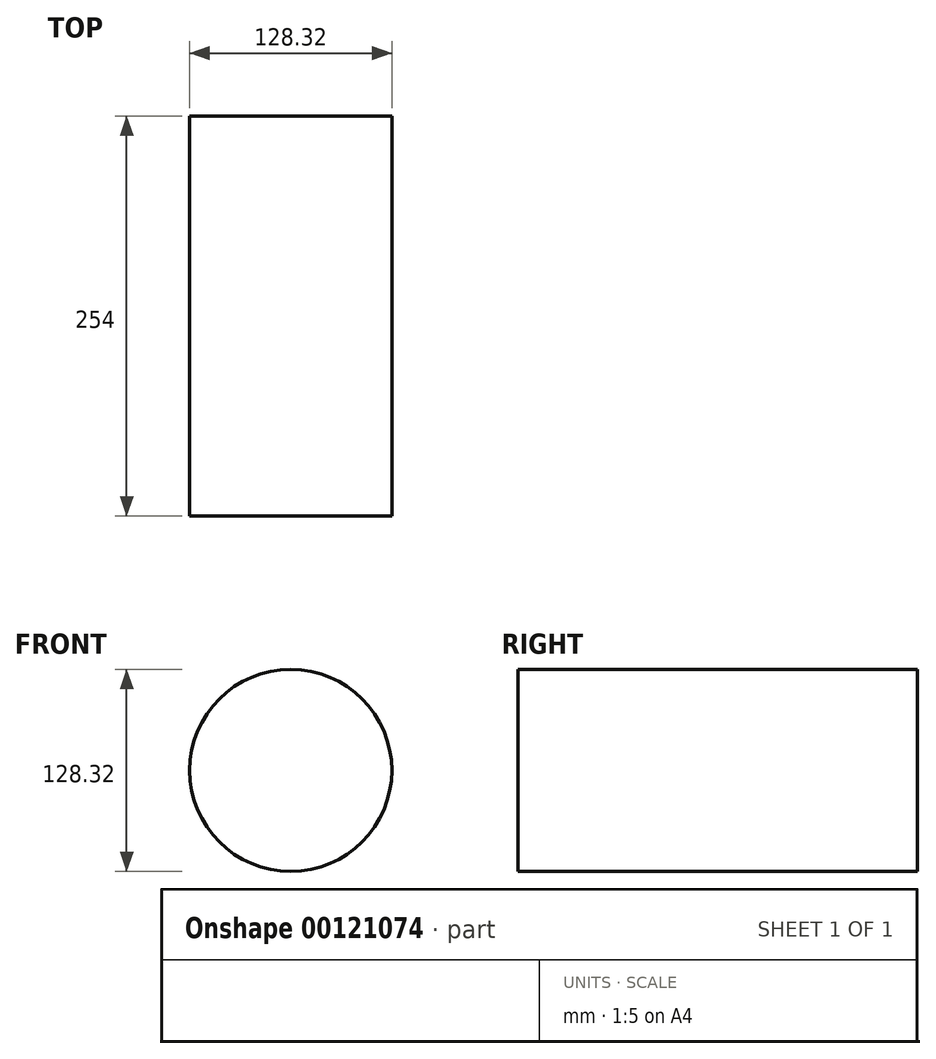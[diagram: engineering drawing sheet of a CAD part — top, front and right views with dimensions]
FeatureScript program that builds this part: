
annotation { "Feature Type Name" : "Feature", "Feature Type Description" : "" }
export const myFeature = defineFeature(function(context is Context, id is Id, definition is map)
    precondition{}
    {
        {
            var Q0;
            Q0=qCreatedBy(makeId("Front.planeOp"),FACE);
            var sketch = newSketch(context, id + "F0", { "sketchPlane" : qUnion([Q0])});
            skCircle(sketch, "E0", {"center": v(0, 0) * mm, "radius": 64.16 * mm});
            skSolve(sketch);
        }
        {
            var Q0;
            Q0=sQuery(id+"F0.wireOp",EDGE,"E0");
            extrude(context, id + "F1", {"bodyType" : ToolBodyType.SURFACE, "surfaceEntities" : qUnion([Q0]), "depth" : 254 * mm});
        }
    });
